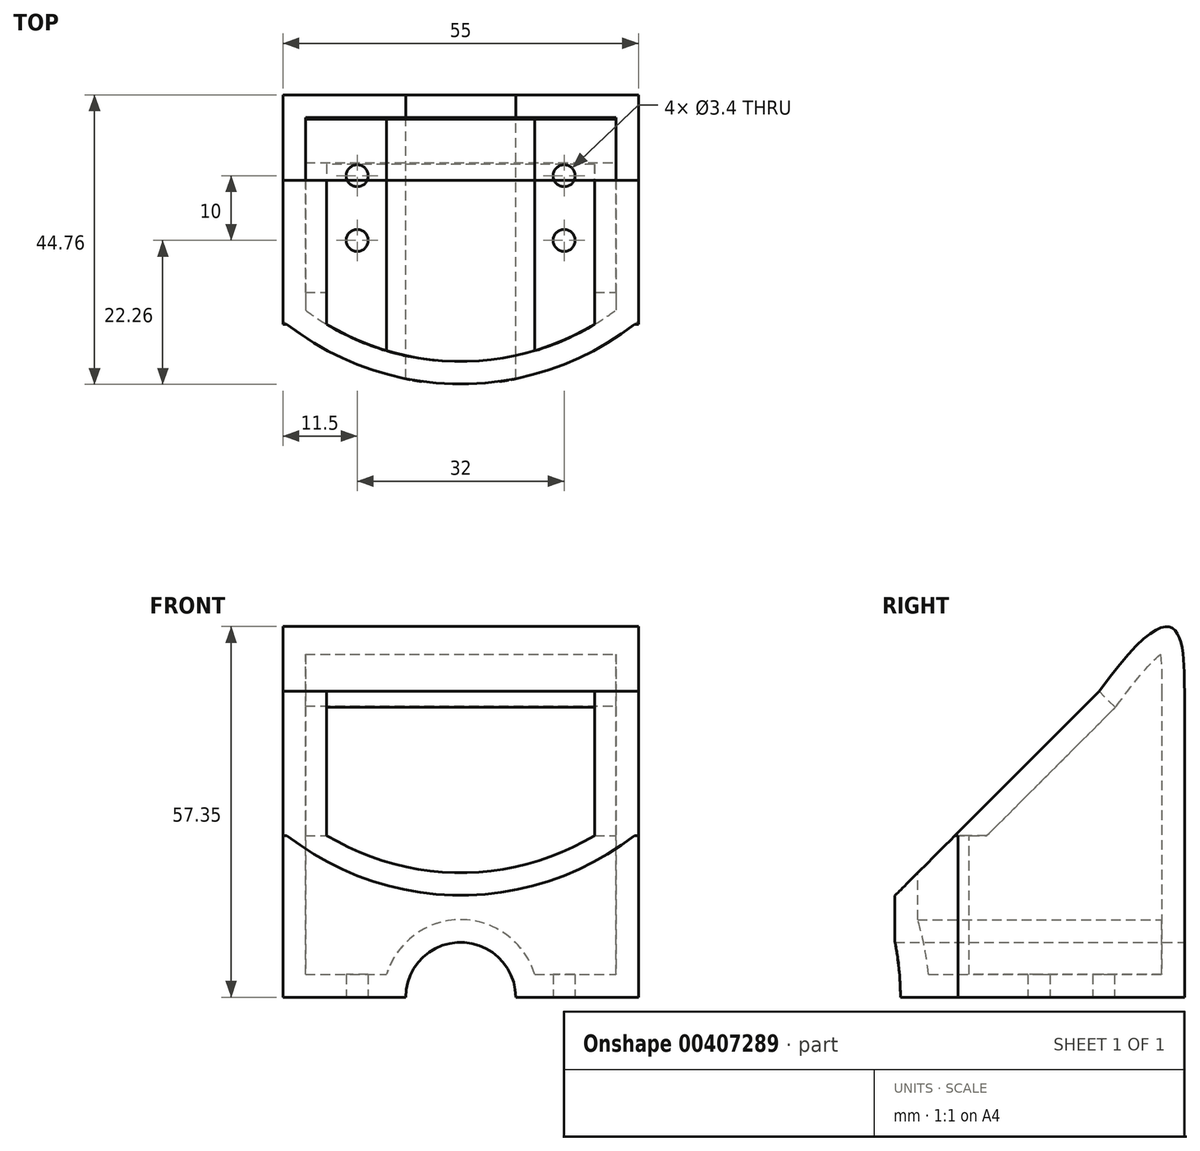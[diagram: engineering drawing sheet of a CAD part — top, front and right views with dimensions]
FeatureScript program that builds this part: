
annotation { "Feature Type Name" : "Feature", "Feature Type Description" : "" }
export const myFeature = defineFeature(function(context is Context, id is Id, definition is map)
    precondition{}
    {
        {
            var Q0;
            Q0=qCreatedBy(makeId("Top.planeOp"),FACE);
            var sketch = newSketch(context, id + "F0", { "sketchPlane" : qUnion([Q0])});
            skLineSegment(sketch, "E0.bottom", {"start": v(0, 0) * mm, "end": v(55, 0) * mm});
            skLineSegment(sketch, "E0.top", {"start": v(0, -45) * mm, "end": v(55, -45) * mm});
            skLineSegment(sketch, "E0.left", {"start": v(0, 0) * mm, "end": v(0, -45) * mm});
            skLineSegment(sketch, "E0.right", {"start": v(55, 0) * mm, "end": v(55, -45) * mm});
            skSolve(sketch);
        }
        {
            var Q0;
            Q0=qSketchRegion(id+"F0",true);
            extrude(context, id + "F1", {"entities" : qUnion([Q0]), "depth" : 25 * mm});
        }
        {
            var Q0;
            Q0=makeQuery(id+"F1.opExtrude","CAP_FACE",FACE,{"disambiguationData":[OSD([sQuery(id+"F0.wireOp",EDGE,"E0.bottom"),sQuery(id+"F0.wireOp",EDGE,"E0.top"),sQuery(id+"F0.wireOp",EDGE,"E0.left"),sQuery(id+"F0.wireOp",EDGE,"E0.right")])],"isStart":false});
            var sketch = newSketch(context, id + "F2", { "sketchPlane" : qUnion([Q0])});
            skLineSegment(sketch, "E1", {"start": v(0, 0) * mm, "end": v(0, -35) * mm});
            skArc(sketch, "E2", {"start": v(0, -35) * mm, "mid": v(27.5, -44.76) * mm, "end": v(55, -35) * mm});
            skSolve(sketch);
        }
        {
            var Q0;
            {var subQ0=sQuery(id+"F2.wireOp",EDGE,"E2");Q0=makeQuery(id+"F2.imprint","IMPRINT",FACE,{"disambiguationData":[TD([[makeQuery(id+"F2.imprint","IMPRINT",EDGE,{"derivedFrom":subQ0}),-1.0]])]});}
            extrude(context, id + "F3", {"entities" : qUnion([Q0]), "operationType" : NewBodyOperationType.REMOVE, "oppositeDirection" : true, "depth" : 25 * mm});
        }
        {
            var Q0;
            Q0=makeQuery(id+"F1.opExtrude","SWEPT_FACE",FACE,{"disambiguationData":[OSD([sQuery(id+"F0.wireOp",EDGE,"E0.bottom")])]});
            var sketch = newSketch(context, id + "F4", { "sketchPlane" : qUnion([Q0])});
            skCircle(sketch, "E3", {"center": v(-27.5, 0) * mm, "radius": 8.5 * mm});
            skSolve(sketch);
        }
        {
            var Q0;
            Q0=qSketchRegion(id+"F4",true);
            extrude(context, id + "F5", {"entities" : qUnion([Q0]), "operationType" : NewBodyOperationType.REMOVE, "oppositeDirection" : true, "depth" : 45 * mm});
        }
        {
            var Q0;
            Q0=makeQuery(id+"F1.opExtrude","CAP_FACE",FACE,{"disambiguationData":[OSD([sQuery(id+"F0.wireOp",EDGE,"E0.bottom"),sQuery(id+"F0.wireOp",EDGE,"E0.top"),sQuery(id+"F0.wireOp",EDGE,"E0.left"),sQuery(id+"F0.wireOp",EDGE,"E0.right")])],"isStart":false});
            shell(context, id + "F6", {"entities" : qUnion([Q0]), "thickness" : 3.5 * mm});
        }
        {
            var Q0;
            {var subQ0=sQuery(id+"F0.wireOp",EDGE,"E0.bottom");var subQ1=sQuery(id+"F0.wireOp",EDGE,"E0.left");Q0=makeQuery(id+"F5.boolean.opBoolean","SPLIT",FACE,{"disambiguationData":[TD([makeQuery(id+"F1.opExtrude","SWEPT_FACE",FACE,{"disambiguationData":[OSD([subQ1])]})])],"derivedFrom":makeQuery(id+"F1.opExtrude","CAP_FACE",FACE,{"disambiguationData":[OSD([subQ0,sQuery(id+"F0.wireOp",EDGE,"E0.top"),subQ1,sQuery(id+"F0.wireOp",EDGE,"E0.right")])],"isStart":true})});}
            var sketch = newSketch(context, id + "F7", { "sketchPlane" : qUnion([Q0])});
            skLineSegment(sketch, "E4", {"start": v(0, 0) * mm, "end": v(0, 17.5) * mm});
            skLineSegment(sketch, "E5", {"start": v(0, 17.5) * mm, "end": v(11.5, 17.5) * mm});
            skLineSegment(sketch, "E6", {"start": v(11.5, 17.5) * mm, "end": v(11.5, 22.5) * mm});
            skLineSegment(sketch, "E7", {"start": v(11.5, 17.5) * mm, "end": v(11.5, 12.5) * mm});
            skCircle(sketch, "E8", {"center": v(11.5, 22.5) * mm, "radius": 1.7 * mm});
            skCircle(sketch, "E9", {"center": v(11.5, 12.5) * mm, "radius": 1.7 * mm});
            skLineSegment(sketch, "E10", {"start": v(0, 0) * mm, "end": v(27.5, 0) * mm});
            skLineSegment(sketch, "E11", {"start": v(27.5, 0) * mm, "end": v(27.5, 6.97) * mm});
            skLineSegment(sketch, "E12.MirrorCS", {"start": v(43.5, 17.5) * mm, "end": v(43.5, 22.5) * mm});
            skLineSegment(sketch, "E13.MirrorCS", {"start": v(43.5, 17.5) * mm, "end": v(43.5, 12.5) * mm});
            skCircle(sketch, "E14.MirrorC", {"center": v(43.5, 22.5) * mm, "radius": 1.7 * mm});
            skCircle(sketch, "E15.MirrorC", {"center": v(43.5, 12.5) * mm, "radius": 1.7 * mm});
            skSolve(sketch);
        }
        {
            var Q0;
            Q0=qSketchRegion(id+"F7",true);
            extrude(context, id + "F8", {"entities" : qUnion([Q0]), "operationType" : NewBodyOperationType.REMOVE, "oppositeDirection" : true, "depth" : 5 * mm});
        }
        {
            var Q0;
            Q0=makeQuery(id+"F1.opExtrude","SWEPT_FACE",FACE,{"disambiguationData":[OSD([sQuery(id+"F0.wireOp",EDGE,"E0.right")])]});
            var sketch = newSketch(context, id + "F9", { "sketchPlane" : qUnion([Q0])});
            skLineSegment(sketch, "E16", {"start": v(0, 0) * mm, "end": v(0, 35) * mm});
            skLineSegment(sketch, "E17", {"start": v(0, 0) * mm, "end": v(-45, 0) * mm});
            skLineSegment(sketch, "E18", {"start": v(-45, 0) * mm, "end": v(-45, 28.63) * mm});
            skLineSegment(sketch, "E19", {"start": v(0, 35) * mm, "end": v(-3.5, 35) * mm});
            skLineSegment(sketch, "E20", {"start": v(-35, 12.5) * mm, "end": v(-35, 15.5) * mm});
            skLineSegment(sketch, "E21", {"start": v(-35, 15.5) * mm, "end": v(-45, 15.5) * mm});
            skLineSegment(sketch, "E22", {"start": v(-45, 15.5) * mm, "end": v(-13.18, 47.32) * mm});
            skLineSegment(sketch, "E23", {"start": v(-13.18, 47.32) * mm, "end": v(0, 47.32) * mm});
            skLineSegment(sketch, "E24", {"start": v(0, 47.32) * mm, "end": v(0, 0) * mm});
            skLineSegment(sketch, "E25", {"start": v(-35, 25) * mm, "end": v(-45, 25) * mm});
            skPoint(sketch, "E26.orphan", {"position": v(0, 60.5) * mm});
            skFitSpline(sketch, "E27", {"points": [v(-13.18, 47.32) * mm, v(0, 47.32) * mm, v(9.04, 29.49) * mm], "startDerivative": vector(88.24, 122.82) * mm, "endDerivative": vector(49.16, -29.96) * mm});
            skSolve(sketch);
        }
        {
            var Q0;
            {var subQ1=sQuery(id+"F9.wireOp",EDGE,"E18");var subQ3=sQuery(id+"F9.wireOp",EDGE,"E25");var subQ4=makeQuery(id+"F9.imprint","INTERSECT",VERTEX,{"derivedFrom":[subQ1,subQ3]});Q0=makeQuery(id+"F9.imprint","IMPRINT",FACE,{"disambiguationData":[TD([[makeQuery(id+"F9.imprint","IMPRINT",EDGE,{"disambiguationData":[TD([[subQ4,1.0]])],"derivedFrom":subQ3}),1.0]])]});}
            extrude(context, id + "F10", {"entities" : qUnion([Q0]), "operationType" : NewBodyOperationType.REMOVE, "oppositeDirection" : true, "depth" : 59.6 * mm, "offsetDistance" : 25 * mm});
        }
        {
            var Q0;
            {var subQ0=sQuery(id+"F9.wireOp",EDGE,"E23");Q0=makeQuery(id+"F9.imprint","IMPRINT",FACE,{"disambiguationData":[TD([[makeQuery(id+"F9.imprint","IMPRINT",EDGE,{"derivedFrom":subQ0}),1.0]])]});}
            var Q1;
            {var subQ6=sQuery(id+"F9.wireOp",EDGE,"E23");Q1=makeQuery(id+"F9.imprint","IMPRINT",FACE,{"disambiguationData":[TD([[makeQuery(id+"F9.imprint","IMPRINT",EDGE,{"derivedFrom":subQ6}),-1.0]])]});}
            extrude(context, id + "F11", {"entities" : qUnion([Q0, Q1]), "operationType" : NewBodyOperationType.ADD, "oppositeDirection" : true, "depth" : 55 * mm, "offsetDistance" : 25 * mm});
        }
        {
            var Q0;
            {var subQ1=sQuery(id+"F0.wireOp",EDGE,"E0.right");Q0=makeQuery(id+"F11.boolean.opBoolean","SPLIT",FACE,{"disambiguationData":[TD([makeQuery(id+"F6.opShell","OFFSET_FACE",FACE,{"disambiguationData":[OSD([sQuery(id+"F0.wireOp",EDGE,"E0.left")])]})])],"derivedFrom":makeQuery(id+"F11.opExtrude","SWEPT_FACE",FACE,{"disambiguationData":[OSD([subQ1,sQuery(id+"F9.wireOp",EDGE,"E25")])]})});}
            shell(context, id + "F12", {"entities" : qUnion([Q0]), "thickness" : 3.5 * mm});
        }
        {
            var Q0;
            {var subQ0=sQuery(id+"F9.wireOp",EDGE,"E22");Q0=makeQuery(id+"F11.boolean.opBoolean","MERGE",FACE,{"derivedFrom":[makeQuery(id+"F10.boolean.opBoolean","COPY",FACE,{"derivedFrom":makeQuery(id+"F10.opExtrude","SWEPT_FACE",FACE,{"disambiguationData":[OSD([subQ0])]})}),makeQuery(id+"F11.opExtrude","SWEPT_FACE",FACE,{"disambiguationData":[OSD([subQ0])]})]});}
            var sketch = newSketch(context, id + "F13", { "sketchPlane" : qUnion([Q0])});
            skLineSegment(sketch, "E28", {"start": v(6.78, -7.42) * mm, "end": v(6.78, 24.14) * mm});
            skLineSegment(sketch, "E29", {"start": v(6.78, 24.14) * mm, "end": v(48.22, 24.14) * mm});
            skLineSegment(sketch, "E30", {"start": v(48.22, 24.14) * mm, "end": v(48.22, -7.42) * mm});
            skLineSegment(sketch, "E31", {"start": v(48.22, -7.42) * mm, "end": v(6.78, -7.42) * mm});
            skSolve(sketch);
        }
        {
            var Q0;
            Q0 = qSketchRegion(id + "F13", true);
            extrude(context, id + "F14", {"entities" : qUnion([Q0]), "operationType" : NewBodyOperationType.REMOVE, "oppositeDirection" : true, "depth" : 5 * mm, "offsetDistance" : 25 * mm});
        }
    });
